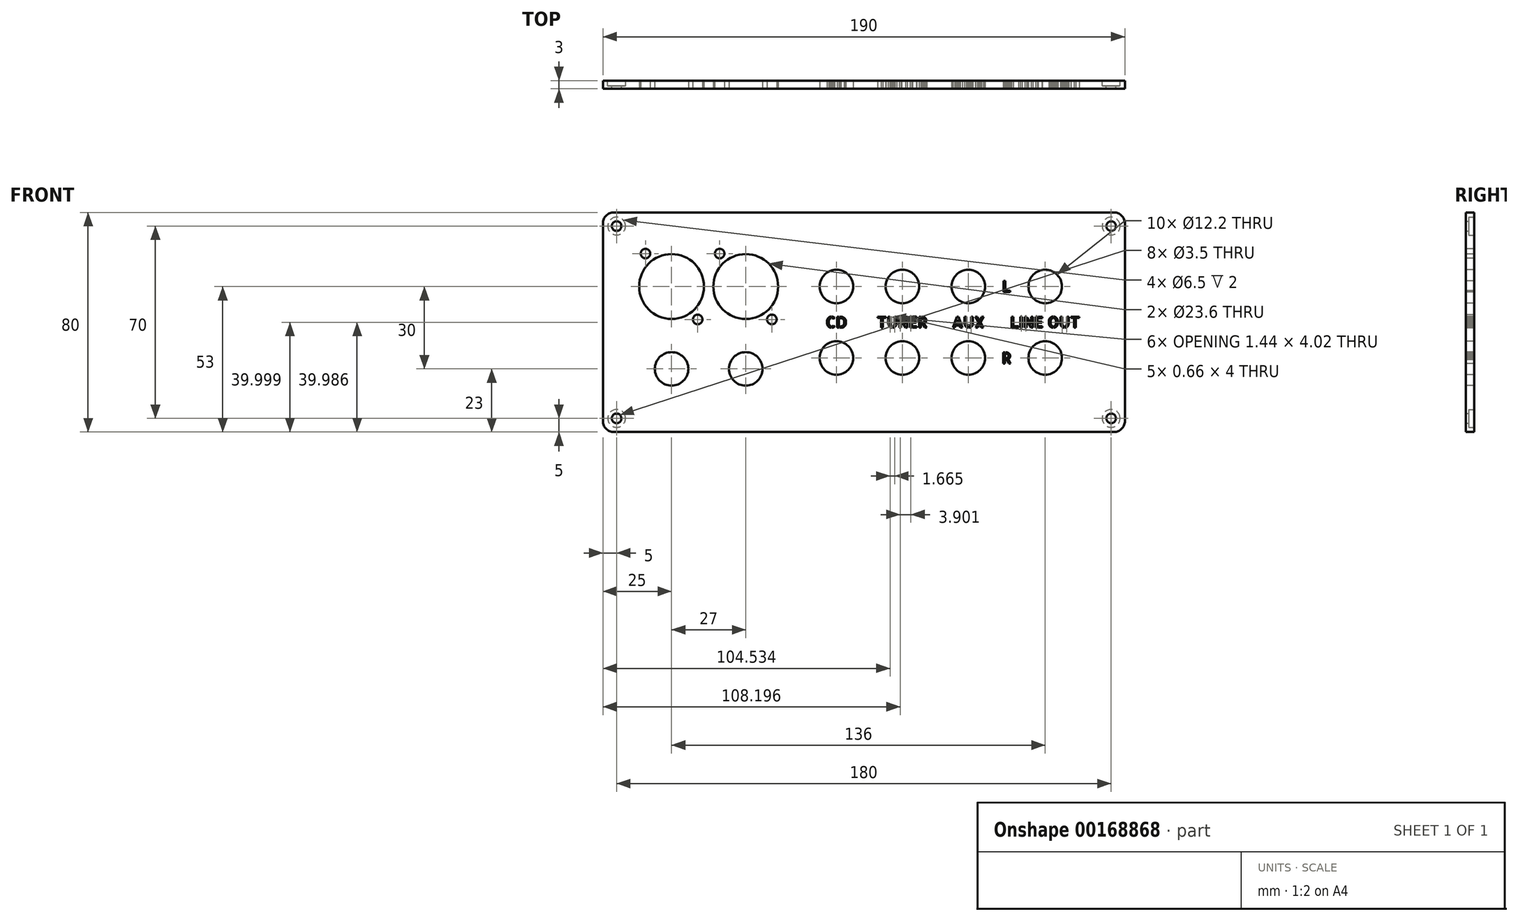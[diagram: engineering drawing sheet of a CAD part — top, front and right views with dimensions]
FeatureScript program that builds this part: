
annotation { "Feature Type Name" : "Feature", "Feature Type Description" : "" }
export const myFeature = defineFeature(function(context is Context, id is Id, definition is map)
    precondition{}
    {
        {
            var Q0;
            Q0=qCreatedBy(makeId("Front.planeOp"),FACE);
            var sketch = newSketch(context, id + "F0", { "sketchPlane" : qUnion([Q0])});
            skLineSegment(sketch, "E0.bottom", {"start": v(91, -40) * mm, "end": v(-91, -40) * mm});
            skLineSegment(sketch, "E0.top", {"start": v(91, 40) * mm, "end": v(-91, 40) * mm});
            skLineSegment(sketch, "E0.left", {"start": v(95, -36) * mm, "end": v(95, 36) * mm});
            skLineSegment(sketch, "E0.right", {"start": v(-95, -36) * mm, "end": v(-95, 36) * mm});
            skPoint(sketch, "E0.middle", {"position": v(0, 0) * mm});
            skLineSegment(sketch, "E1", {"start": v(-85.71, 13) * mm, "end": v(95.6, 13) * mm, "construction": true});
            skLineSegment(sketch, "E2", {"start": v(-95.37, 0) * mm, "end": v(94.03, 0) * mm, "construction": true});
            skLineSegment(sketch, "E3.MirrorCS", {"start": v(-85.71, -13) * mm, "end": v(95.6, -13) * mm, "construction": true});
            skLineSegment(sketch, "E4", {"start": v(-43, 41.44) * mm, "end": v(-43, -47.3) * mm, "construction": true});
            skLineSegment(sketch, "E5", {"start": v(-10, 39.64) * mm, "end": v(-10, -46.86) * mm, "construction": true});
            skLineSegment(sketch, "E6", {"start": v(38, 40.32) * mm, "end": v(38, -46.63) * mm, "construction": true});
            skLineSegment(sketch, "E7", {"start": v(66, 41.22) * mm, "end": v(66, -44.39) * mm, "construction": true});
            skCircle(sketch, "E8", {"center": v(-70, -17) * mm, "radius": 6.1 * mm});
            skCircle(sketch, "E9", {"center": v(-10, 13) * mm, "radius": 6.1 * mm});
            skCircle(sketch, "E10", {"center": v(14, 13) * mm, "radius": 6.1 * mm});
            skCircle(sketch, "E11", {"center": v(38, 13) * mm, "radius": 6.1 * mm});
            skCircle(sketch, "E12", {"center": v(66, 13) * mm, "radius": 6.1 * mm});
            skCircle(sketch, "E13", {"center": v(66, -13) * mm, "radius": 6.1 * mm});
            skCircle(sketch, "E14", {"center": v(38, -13) * mm, "radius": 6.1 * mm});
            skCircle(sketch, "E15", {"center": v(14, -13) * mm, "radius": 6.1 * mm});
            skCircle(sketch, "E16", {"center": v(-10, -13) * mm, "radius": 6.1 * mm});
            skCircle(sketch, "E17", {"center": v(-43, -17) * mm, "radius": 6.1 * mm});
            skPoint(sketch, "E18.visualSharp", {"position": v(-95, 40) * mm});
            skArc(sketch, "E18.filletArc", {"start": v(-91, 40) * mm, "mid": v(-93.83, 38.83) * mm, "end": v(-95, 36) * mm});
            skPoint(sketch, "E19.visualSharp", {"position": v(95, 40) * mm});
            skArc(sketch, "E19.filletArc", {"start": v(95, 36) * mm, "mid": v(93.83, 38.83) * mm, "end": v(91, 40) * mm});
            skPoint(sketch, "E20.visualSharp", {"position": v(95, -40) * mm});
            skArc(sketch, "E20.filletArc", {"start": v(91, -40) * mm, "mid": v(93.83, -38.83) * mm, "end": v(95, -36) * mm});
            skPoint(sketch, "E21.visualSharp", {"position": v(-95, -40) * mm});
            skArc(sketch, "E21.filletArc", {"start": v(-95, -36) * mm, "mid": v(-93.83, -38.83) * mm, "end": v(-91, -40) * mm});
            skLineSegment(sketch, "E22", {"start": v(14, 33.36) * mm, "end": v(14, -26.92) * mm, "construction": true});
            skLineSegment(sketch, "E23", {"start": v(-70, 17.5) * mm, "end": v(-70, -27.72) * mm, "construction": true});
            skCircle(sketch, "E24", {"center": v(-70, 13) * mm, "radius": 11.8 * mm});
            skPoint(sketch, "E25.middle", {"position": v(-43, 13) * mm});
            skCircle(sketch, "E26", {"center": v(-43, 13) * mm, "radius": 11.8 * mm});
            skLineSegment(sketch, "E27", {"start": v(-79.5, 31.15) * mm, "end": v(-79.5, -6.01) * mm, "construction": true});
            skLineSegment(sketch, "E28", {"start": v(-85.78, 25) * mm, "end": v(-56.54, 25) * mm, "construction": true});
            skLineSegment(sketch, "E29", {"start": v(-56.54, 25) * mm, "end": v(-28.92, 25) * mm, "construction": true});
            skLineSegment(sketch, "E30", {"start": v(-52.5, 30.05) * mm, "end": v(-52.5, -0.68) * mm, "construction": true});
            skLineSegment(sketch, "E31.MirrorCS", {"start": v(-60.5, 31.15) * mm, "end": v(-60.5, -6.01) * mm, "construction": true});
            skLineSegment(sketch, "E32.MirrorCS", {"start": v(-85.78, 1) * mm, "end": v(-56.54, 1) * mm, "construction": true});
            skLineSegment(sketch, "E33.MirrorCS", {"start": v(-56.54, 1) * mm, "end": v(-28.92, 1) * mm, "construction": true});
            skLineSegment(sketch, "E34.MirrorCS", {"start": v(-33.5, 30.05) * mm, "end": v(-33.5, -0.68) * mm, "construction": true});
            skPoint(sketch, "E35", {"position": v(-79.5, 25) * mm});
            skPoint(sketch, "E36", {"position": v(-60.5, 1) * mm});
            skPoint(sketch, "E37", {"position": v(-52.5, 25) * mm});
            skPoint(sketch, "E38", {"position": v(-33.5, 1) * mm});
            skLineSegment(sketch, "E39", {"start": v(-82.1, -17) * mm, "end": v(-31.97, -17) * mm, "construction": true});
            skSolve(sketch);
        }
        {
            var Q0;
            Q0=qSketchRegion(id+"F0",true);
            var Q1;
            Q1=makeQuery(id+"F0.imprint","IMPRINT",FACE,{"disambiguationData":[TD([[makeQuery(id+"F0.imprint","IMPRINT",EDGE,{"derivedFrom":sQuery(id+"F0.wireOp",EDGE,"E24")}),-1.0]])]});
            var Q2;
            Q2=makeQuery(id+"F0.imprint","IMPRINT",FACE,{"disambiguationData":[TD([[makeQuery(id+"F0.imprint","IMPRINT",EDGE,{"derivedFrom":sQuery(id+"F0.wireOp",EDGE,"E25.bottom")}),-1.0]])]});
            extrude(context, id + "F1", {"entities" : qUnion([Q0, Q1, Q2]), "oppositeDirection" : true, "depth" : 3 * mm});
        }
        {
            var Q0;
            Q0=makeQuery(id+"F1.opExtrude","CAP_FACE",FACE,{"disambiguationData":[OSD([sQuery(id+"F0.wireOp",EDGE,"E0.bottom"),sQuery(id+"F0.wireOp",EDGE,"E0.top"),sQuery(id+"F0.wireOp",EDGE,"E0.left"),sQuery(id+"F0.wireOp",EDGE,"E0.right"),sQuery(id+"F0.wireOp",EDGE,"E8"),sQuery(id+"F0.wireOp",EDGE,"E9"),sQuery(id+"F0.wireOp",EDGE,"E10"),sQuery(id+"F0.wireOp",EDGE,"E11"),sQuery(id+"F0.wireOp",EDGE,"E12"),sQuery(id+"F0.wireOp",EDGE,"E13"),sQuery(id+"F0.wireOp",EDGE,"E14"),sQuery(id+"F0.wireOp",EDGE,"E15"),sQuery(id+"F0.wireOp",EDGE,"E16"),sQuery(id+"F0.wireOp",EDGE,"E17"),sQuery(id+"F0.wireOp",EDGE,"E18.filletArc"),sQuery(id+"F0.wireOp",EDGE,"E19.filletArc"),sQuery(id+"F0.wireOp",EDGE,"E20.filletArc"),sQuery(id+"F0.wireOp",EDGE,"E21.filletArc")])],"isStart":false});
            var sketch = newSketch(context, id + "F2", { "sketchPlane" : qUnion([Q0])});
            skLineSegment(sketch, "E40", {"start": v(-103.47, 35) * mm, "end": v(120, 35) * mm, "construction": true});
            skLineSegment(sketch, "E41", {"start": v(-90, 42.73) * mm, "end": v(-90, -48.6) * mm, "construction": true});
            skLineSegment(sketch, "E42.MirrorCS", {"start": v(90, 42.73) * mm, "end": v(90, -48.6) * mm, "construction": true});
            skLineSegment(sketch, "E43.MirrorCS", {"start": v(-103.47, -35) * mm, "end": v(120, -35) * mm, "construction": true});
            skPoint(sketch, "E44", {"position": v(-90, 35) * mm});
            skPoint(sketch, "E45", {"position": v(90, 35) * mm});
            skPoint(sketch, "E46", {"position": v(90, -35) * mm});
            skPoint(sketch, "E47", {"position": v(-90, -35) * mm});
            skSolve(sketch);
        }
        {
            var Q0;
            Q0=sQuery(id+"F2.wireOp",VERTEX,"E44");
            var Q1;
            Q1=sQuery(id+"F2.wireOp",VERTEX,"E45");
            var Q2;
            Q2=sQuery(id+"F2.wireOp",VERTEX,"E46");
            var Q3;
            Q3=sQuery(id+"F2.wireOp",VERTEX,"E47");
            var Q4;
            Q4=makeQuery(id+"F1.opExtrude","SWEPT_BODY",BODY,{"disambiguationData":[OSD([sQuery(id+"F0.wireOp",EDGE,"E0.bottom"),sQuery(id+"F0.wireOp",EDGE,"E0.top"),sQuery(id+"F0.wireOp",EDGE,"E0.left"),sQuery(id+"F0.wireOp",EDGE,"E0.right"),sQuery(id+"F0.wireOp",EDGE,"E8"),sQuery(id+"F0.wireOp",EDGE,"E9"),sQuery(id+"F0.wireOp",EDGE,"E10"),sQuery(id+"F0.wireOp",EDGE,"E11"),sQuery(id+"F0.wireOp",EDGE,"E12"),sQuery(id+"F0.wireOp",EDGE,"E13"),sQuery(id+"F0.wireOp",EDGE,"E14"),sQuery(id+"F0.wireOp",EDGE,"E15"),sQuery(id+"F0.wireOp",EDGE,"E16"),sQuery(id+"F0.wireOp",EDGE,"E17"),sQuery(id+"F0.wireOp",EDGE,"E18.filletArc"),sQuery(id+"F0.wireOp",EDGE,"E19.filletArc"),sQuery(id+"F0.wireOp",EDGE,"E20.filletArc"),sQuery(id+"F0.wireOp",EDGE,"E21.filletArc")])]});
            hole(context, id + "F3", {"style" : HoleStyle.C_BORE, "endStyle" : HoleEndStyle.THROUGH, "holeDiameter" : 3.5 * mm, "cBoreDiameter" : 6.5 * mm, "cBoreDepth" : 2 * mm, "startFromSketch" : true, "locations" : qUnion([Q0, Q1, Q2, Q3]), "scope" : qUnion([Q4]), "isTappedThrough" : true});
        }
        {
            var Q0;
            Q0=makeQuery(id+"F1.opExtrude","CAP_FACE",FACE,{"disambiguationData":[OSD([sQuery(id+"F0.wireOp",EDGE,"E0.bottom"),sQuery(id+"F0.wireOp",EDGE,"E0.top"),sQuery(id+"F0.wireOp",EDGE,"E0.left"),sQuery(id+"F0.wireOp",EDGE,"E0.right"),sQuery(id+"F0.wireOp",EDGE,"E8"),sQuery(id+"F0.wireOp",EDGE,"E9"),sQuery(id+"F0.wireOp",EDGE,"E10"),sQuery(id+"F0.wireOp",EDGE,"E11"),sQuery(id+"F0.wireOp",EDGE,"E12"),sQuery(id+"F0.wireOp",EDGE,"E13"),sQuery(id+"F0.wireOp",EDGE,"E14"),sQuery(id+"F0.wireOp",EDGE,"E15"),sQuery(id+"F0.wireOp",EDGE,"E16"),sQuery(id+"F0.wireOp",EDGE,"E17"),sQuery(id+"F0.wireOp",EDGE,"E18.filletArc"),sQuery(id+"F0.wireOp",EDGE,"E19.filletArc"),sQuery(id+"F0.wireOp",EDGE,"E20.filletArc"),sQuery(id+"F0.wireOp",EDGE,"E21.filletArc")])],"isStart":true});
            var sketch = newSketch(context, id + "F4", { "sketchPlane" : qUnion([Q0])});
            skLineSegment(sketch, "E48", {"start": v(-70, 25.45) * mm, "end": v(-70, -28.4) * mm, "construction": true});
            skLineSegment(sketch, "E49", {"start": v(-10, 30.05) * mm, "end": v(-10, -28.76) * mm, "construction": true});
            skLineSegment(sketch, "E50", {"start": v(14, 30.78) * mm, "end": v(14, -30.42) * mm, "construction": true});
            skLineSegment(sketch, "E51", {"start": v(38, 30.97) * mm, "end": v(38, -28.76) * mm, "construction": true});
            skLineSegment(sketch, "E52", {"start": v(66, 29.81) * mm, "end": v(66, -30.6) * mm, "construction": true});
            skLineSegment(sketch, "E53", {"start": v(52, 24.53) * mm, "end": v(52, -25.45) * mm, "construction": true});
            skLineSegment(sketch, "E54", {"start": v(38, -13) * mm, "end": v(66, -13) * mm, "construction": true});
            skLineSegment(sketch, "E55", {"start": v(38, 13) * mm, "end": v(66, 13) * mm, "construction": true});
            skText(sketch, "E56", { "text": "CD", "fontName": "AllertaStencil-Regular.ttf"});
            skText(sketch, "E57", { "text": "TUNER", "fontName": "AllertaStencil-Regular.ttf"});
            skText(sketch, "E58", { "text": "AUX", "fontName": "AllertaStencil-Regular.ttf"});
            skText(sketch, "E59", { "text": "L", "fontName": "AllertaStencil-Regular.ttf"});
            skText(sketch, "E60", { "text": "R", "fontName": "AllertaStencil-Regular.ttf"});
            skText(sketch, "E61", { "text": "LINE OUT", "fontName": "AllertaStencil-Regular.ttf"});
            const initialGuessF4  = {"E56": [-0.01388, -0.002, 1, 0, 0.004], "E57": [0.00477, -0.002, 1, 0, 0.004], "E58": [0.03205, -0.002, 1, 0, 0.004], "E59": [0.05031, 0.011, 1, 0, 0.004], "E60": [0.05021, -0.015, 1, 0, 0.004], "E61": [0.05326, -0.002, 1, 0, 0.004]};
            skSetInitialGuess(sketch, initialGuessF4);
            skSolve(sketch);
        }
        {
            var Q0;
            Q0=qSketchRegion(id+"F4",true);
            extrude(context, id + "F5", {"entities" : qUnion([Q0]), "operationType" : NewBodyOperationType.REMOVE, "endBound" : BoundingType.THROUGH_ALL, "oppositeDirection" : true, "depth" : 0.3 * mm});
        }
        {
            var Q0;
            Q0=sQuery(id+"F0.wireOp",VERTEX,"E35");
            var Q1;
            Q1=sQuery(id+"F0.wireOp",VERTEX,"E36");
            var Q2;
            Q2=sQuery(id+"F0.wireOp",VERTEX,"E37");
            var Q3;
            Q3=sQuery(id+"F0.wireOp",VERTEX,"E38");
            var Q4;
            Q4=makeQuery(id+"F1.opExtrude","SWEPT_BODY",BODY,{"disambiguationData":[OSD([sQuery(id+"F0.wireOp",EDGE,"E0.bottom"),sQuery(id+"F0.wireOp",EDGE,"E0.top"),sQuery(id+"F0.wireOp",EDGE,"E0.left"),sQuery(id+"F0.wireOp",EDGE,"E0.right"),sQuery(id+"F0.wireOp",EDGE,"E8"),sQuery(id+"F0.wireOp",EDGE,"E9"),sQuery(id+"F0.wireOp",EDGE,"E10"),sQuery(id+"F0.wireOp",EDGE,"E11"),sQuery(id+"F0.wireOp",EDGE,"E12"),sQuery(id+"F0.wireOp",EDGE,"E13"),sQuery(id+"F0.wireOp",EDGE,"E14"),sQuery(id+"F0.wireOp",EDGE,"E15"),sQuery(id+"F0.wireOp",EDGE,"E16"),sQuery(id+"F0.wireOp",EDGE,"E17"),sQuery(id+"F0.wireOp",EDGE,"E18.filletArc"),sQuery(id+"F0.wireOp",EDGE,"E19.filletArc"),sQuery(id+"F0.wireOp",EDGE,"E20.filletArc"),sQuery(id+"F0.wireOp",EDGE,"E21.filletArc"),sQuery(id+"F0.wireOp",EDGE,"E24"),sQuery(id+"F0.wireOp",EDGE,"E26")])]});
            hole(context, id + "F6", {"style" : HoleStyle.SIMPLE, "endStyle" : HoleEndStyle.THROUGH, "holeDiameter" : 3.5 * mm, "locations" : qUnion([Q0, Q1, Q2, Q3]), "scope" : qUnion([Q4]), "isTappedThrough" : true});
        }
    });
